# Revit family: Control_Equipment-Lutron-Athena_LTE_Modem
name_source: partatom
category: Lighting Devices
revit_build: Autodesk Revit 2018 (Build: 20190510_1515(x64)
units: mm (PartAtom-declared; Revit-internal decimal feet)

## family parameters
Always vertical = Yes
Cut with Voids When Loaded = No
Maintain Annotation Orientation = No
OmniClass Number = 23.85.80.11.27
OmniClass Title = Lighting Controls
Part Type = Normal
Room Calculation Point = No
Round Connector Dimension = Use Diameter
Shared = No
Work Plane-Based = No

## types (1)
- LUT-LTE-1
    Apparent Load = 18 VA
    Assembly Code = D5020200
    Description = Control Equipment
    Environment = Operating Temperature -20˚ to 40˚C, Storage Temperature -20˚ to 80˚C, Humidity 0 - 95%, Non-condensing, Certification UL, cUL, FCC Class B, RoHS, Location UL Damp Location, IP20
    Finish = Plastic - Lutron - White
    Frequency = 5 Hz
    Height = 7"
    Imput Voltage = 18 V
    Instruction Sheet Link = Contact Lutron for Instruction Sheet Link
    Length = 5 19/32"
    Manufacturer = Lutron Electronics Co., Inc
    Manufacturer Fax Number = 610-282-1243
    Maximum Operating Temperature = 104 °F
    Minimum Operating Temperature = 32 °F
    Model = LUT-LTE-1
    Performance URL = Contact Lutron for Performance Data
    Product Documentation Link = https://www.lutron.com
    Product Name = LTE Modem
    Product Page URL = https://www.lutron.com
    Series = Athena
    URL = http://www.lutron.com
    Version = 2018 - v1.0a
    Video Link = https://www.youtube.com
    Voltage = 18 V
    Voltage Comment = 18 V-, 1 A | 2 x 2 MIMO 2.4/5 GHz: 802.11 b/g/n 2.4 GHz;
802.11 n/a/ac 5 GHz.
    Warranty URL = http://www.lutron.com
    Width = 5 1/32"

## geometry (parser evidence)
native form markers: Sweep x2
no freeform markers — native parametric forms only
